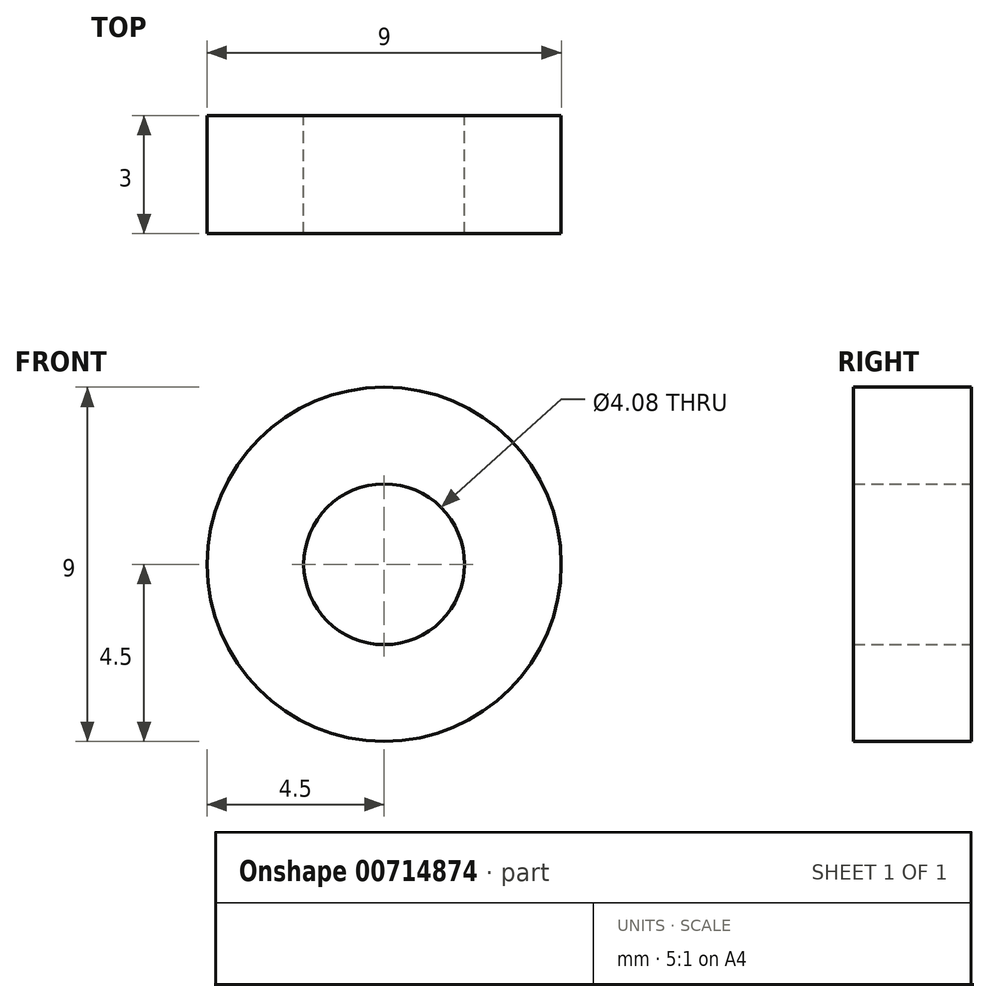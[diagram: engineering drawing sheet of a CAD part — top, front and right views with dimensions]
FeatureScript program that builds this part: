
annotation { "Feature Type Name" : "Feature", "Feature Type Description" : "" }
export const myFeature = defineFeature(function(context is Context, id is Id, definition is map)
    precondition{}
    {
        {
            var Q0;
            Q0=qCreatedBy(makeId("Front.planeOp"),FACE);
            var sketch = newSketch(context, id + "F0", { "sketchPlane" : qUnion([Q0])});
            skCircle(sketch, "E0", {"center": v(0, 0) * mm, "radius": 4.5 * mm});
            skCircle(sketch, "E1", {"center": v(0, 0) * mm, "radius": 2.04 * mm});
            skCircle(sketch, "E2", {"center": v(0, 0) * mm, "radius": 0.55 * mm});
            skLineSegment(sketch, "E3", {"start": v(0.1, 0.54) * mm, "end": v(0.1, -0.54) * mm});
            skLineSegment(sketch, "E4", {"start": v(-0.1, -0.54) * mm, "end": v(-0.1, 0.54) * mm});
            skSolve(sketch);
        }
        {
            var Q0;
            Q0 = qSketchRegion(id + "F0", true);
            extrude(context, id + "F1", {"entities" : qUnion([Q0]), "depth" : 3 * mm, "offsetDistance" : 25 * mm});
        }
    });
